# Revit family: LBP6
name_source: partatom
category: Lighting Fixtures
revit_build: Autodesk Revit 2014 (Build: 20130308_1515(x64)
units: mm (PartAtom-declared; Revit-internal decimal feet)

## types (1)
- LiteBox 6''
    Apparent Load = 0 VA
    Backbox = Hubbell - Aluminium
    Color Filter = 16777215
    Default Elevation = 48"
    Description = LED Downlight Module
    Dimming Lamp Color Temperature Shift = <None>
    Emit Shape Visible in Rendering = No
    Emit from Circle Diameter = 6"
    Glass = Hubbell- Glass Cover
    Is 120V = Yes
    Is 270V = No
    Lamp = LED Downlight
    Load Classification = Lighting
    Manufacturer = Prescolite Lighting
    Model = LBP6
    Photometric Web File = LB6LEDA10L - 35K.ies
    Product Documentation Link = https://hubbellcdn.com
    Product Page URL = https://www.hubbell.com
    Reflector = Hubbell - White
    Tilt Angle = -90.00°
    URL = https://www.hubbell.com
    Voltage = 120 V
    Wattage Comments = 10-20W
    Wire = Hubbell - Wire Finish

## geometry (parser evidence)
native form markers: Blend x2, Sweep x6
no freeform markers — native parametric forms only
